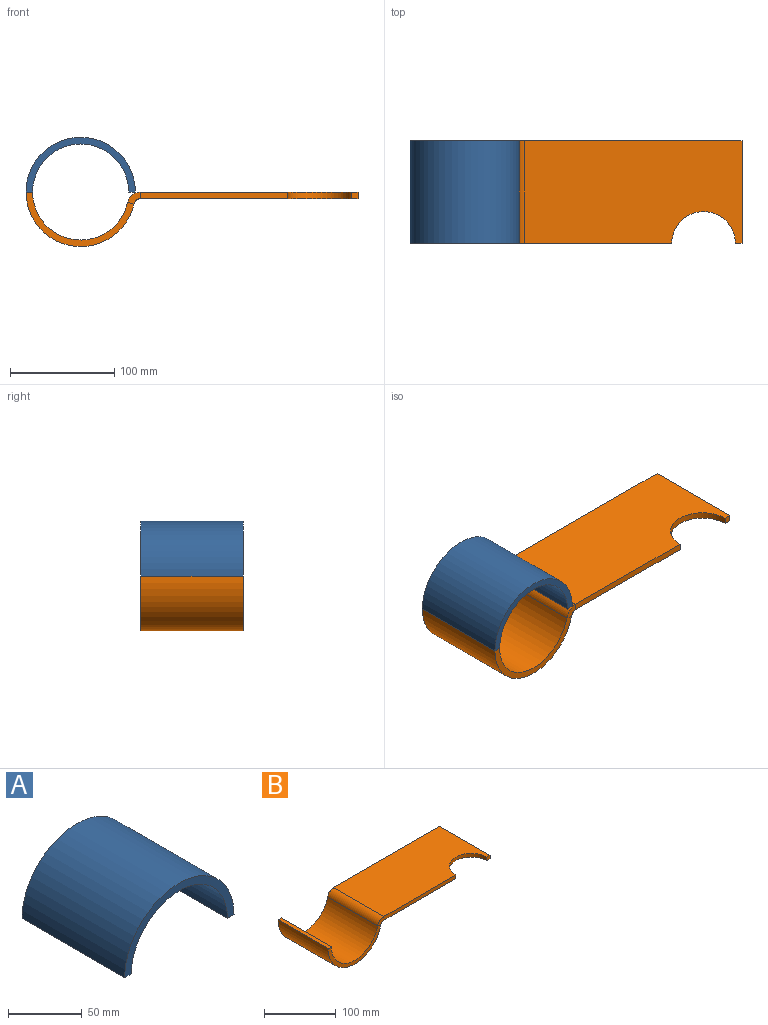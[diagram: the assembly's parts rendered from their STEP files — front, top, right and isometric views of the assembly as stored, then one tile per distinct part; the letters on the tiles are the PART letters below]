
ASSEMBLY  parts=2 mates=1
PART A: 6 faces, bbox 104.8x98.4x52.4 mm
  f0: plane 98.43x6.35mm, normal (0,0,-1), area 625mm2, adj f1,f3,f4,f5
  f1: plane 104.78x52.39mm, normal (0,-1,0), area 981.7mm2, adj f0,f2,f4,f5
  f2: plane 98.43x6.35mm, normal (0,0,-1), area 625mm2, adj f1,f3,f4,f5
  f3: plane 104.78x52.39mm, normal (0,1,0), area 981.7mm2, adj f0,f2,f4,f5
  f4: cylinder r=46.04mm len=98.43mm, axis (0,1,0), area 14235.3mm2, adj f0,f1,f2,f3
  f5: cylinder r=52.39mm len=104.78mm, axis (0,1,0), area 16198.8mm2, adj f0,f1,f2,f3
PART B: 16 faces, bbox 318.1x98.4x52.4 mm
  f0: plane 98.43x6.35mm, normal (1,0,0), area 625mm2, adj f1,f4,f5,f6
  f1: plane 208.4x6.35mm, normal (0,1,0), area 1323.3mm2, adj f0,f5,f6,f13
  f2: plane 141.09x6.35mm, normal (0,-1,0), area 895.9mm2, adj f3,f5,f6,f12
  f3: cylinder r=30.48mm len=60.96mm, axis (0,0,1), area 608mm2, adj f2,f4,f5,f6
  f4: plane 6.35x6.35mm, normal (0,-1,0), area 40.3mm2, adj f0,f3,f5,f6
  f5: plane 208.4x98.43mm, normal (0,0,1), area 19052.4mm2, adj f0,f1,f2,f3,f4,f14
  f6: plane 208.4x98.43mm, normal (0,0,-1), area 19052.4mm2, adj f0,f1,f2,f3,f4,f15
  f7: plane 103.54x52.39mm, normal (0,1,0), area 913.6mm2, adj f8,f10,f11,f13
  f8: plane 98.43x6.35mm, normal (0,0,1), area 625mm2, adj f7,f9,f10,f11
  f9: plane 103.54x52.39mm, normal (0,-1,0), area 913.6mm2, adj f8,f10,f11,f12
  f10: cylinder r=46.04mm len=98.43mm, axis (0,-1,0), area 13247.8mm2, adj f7,f8,f9,f14
  f11: cylinder r=52.39mm len=103.54mm, axis (0,-1,0), area 15075.1mm2, adj f7,f8,f9,f15
  f12: plane 12.4x11.33mm, normal (0,-1,0), area 81.8mm2, adj f2,f9,f14,f15
  f13: plane 12.4x11.33mm, normal (0,1,0), area 81.8mm2, adj f1,f7,f14,f15
  f14: cylinder r=12.7mm len=98.43mm, axis (0,-1,0), area 1691.1mm2, adj f5,f10,f12,f13
  f15: cylinder r=6.35mm len=98.43mm, axis (0,-1,0), area 845.5mm2, adj f6,f11,f12,f13
PLACE A t=(92.32,-29.89,45.55)mm
PLACE B t=(92.32,-29.89,45.55)mm
MATE fastened A.f2 <-> B.f8  axis (0,0,-1) through (-321.56,-128.31,51.02)mm
